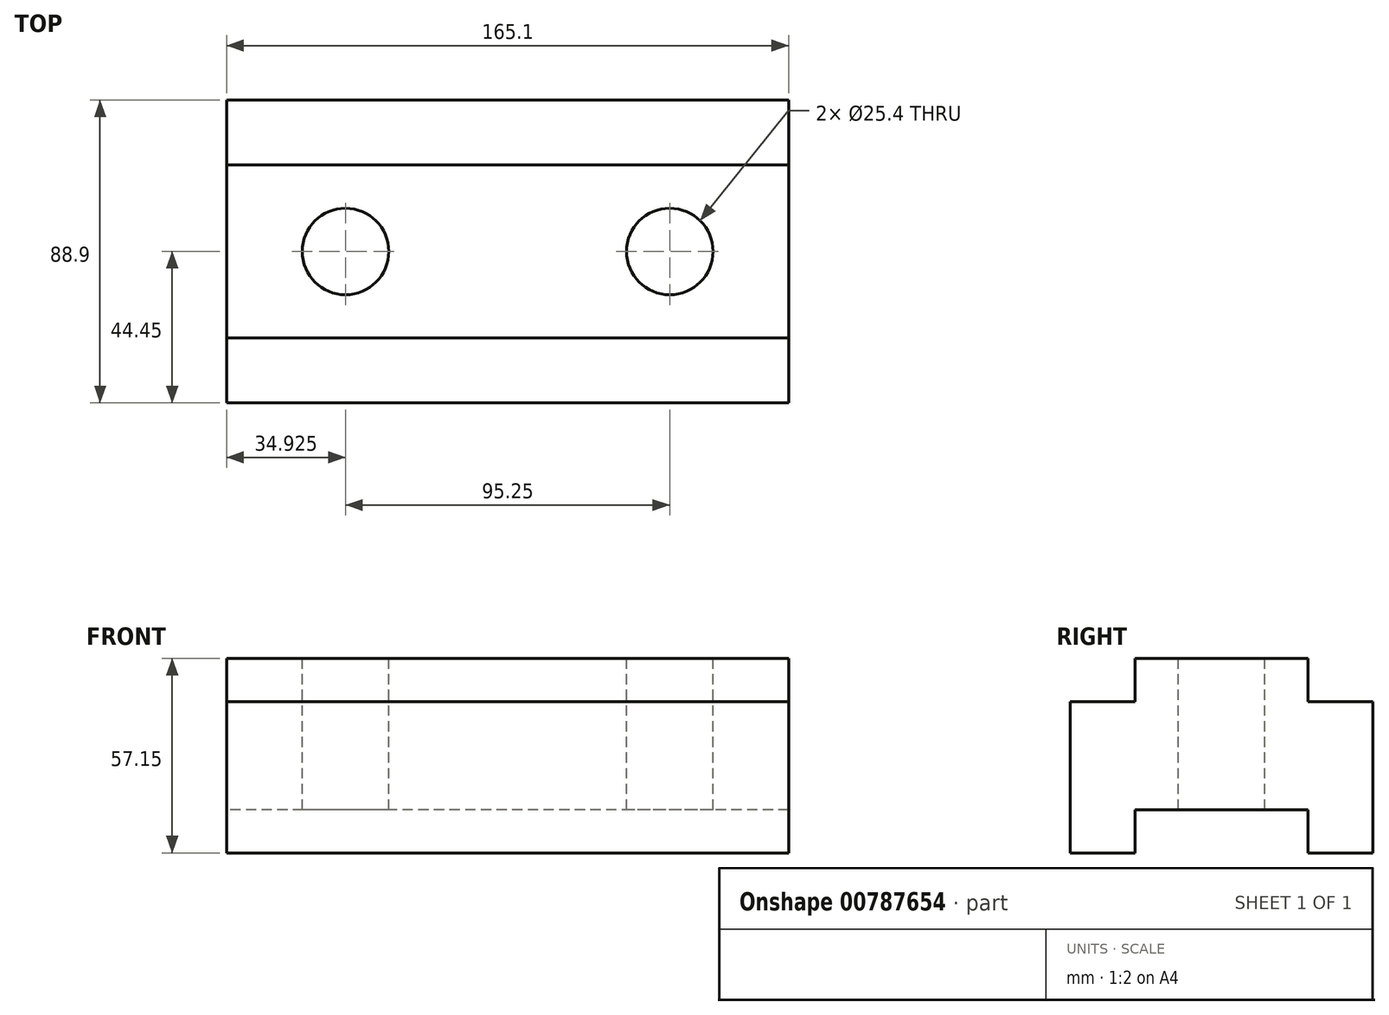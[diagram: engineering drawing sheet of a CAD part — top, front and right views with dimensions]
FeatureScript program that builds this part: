
annotation { "Feature Type Name" : "Feature", "Feature Type Description" : "" }
export const myFeature = defineFeature(function(context is Context, id is Id, definition is map)
    precondition{}
    {
        {
            var Q0;
            Q0=qCreatedBy(makeId("Right.planeOp"),FACE);
            var sketch = newSketch(context, id + "F0", { "sketchPlane" : qUnion([Q0])});
            skLineSegment(sketch, "E0", {"start": v(0, 0) * mm, "end": v(19.05, 0) * mm});
            skLineSegment(sketch, "E1", {"start": v(19.05, 0) * mm, "end": v(19.05, 12.7) * mm});
            skLineSegment(sketch, "E2", {"start": v(19.05, 12.7) * mm, "end": v(69.85, 12.7) * mm});
            skLineSegment(sketch, "E3", {"start": v(69.85, 12.7) * mm, "end": v(69.85, 0) * mm});
            skLineSegment(sketch, "E4", {"start": v(69.85, 0) * mm, "end": v(88.9, 0) * mm});
            skLineSegment(sketch, "E5", {"start": v(88.9, 0) * mm, "end": v(88.9, 44.45) * mm});
            skLineSegment(sketch, "E6", {"start": v(88.9, 44.45) * mm, "end": v(69.85, 44.45) * mm});
            skLineSegment(sketch, "E7", {"start": v(69.85, 44.45) * mm, "end": v(69.85, 57.15) * mm});
            skLineSegment(sketch, "E8", {"start": v(69.85, 57.15) * mm, "end": v(19.05, 57.15) * mm});
            skLineSegment(sketch, "E9", {"start": v(19.05, 57.15) * mm, "end": v(19.05, 44.45) * mm});
            skLineSegment(sketch, "E10", {"start": v(19.05, 44.45) * mm, "end": v(0, 44.45) * mm});
            skLineSegment(sketch, "E11", {"start": v(0, 44.45) * mm, "end": v(0, 0) * mm});
            skSolve(sketch);
        }
        {
            var Q0;
            Q0 = qSketchRegion(id + "F0", true);
            extrude(context, id + "F1", {"entities" : qUnion([Q0]), "depth" : 165.1 * mm, "offsetDistance" : 25.4 * mm});
        }
        {
            var Q0;
            Q0=makeQuery(id+"F1.opExtrude","SWEPT_FACE",FACE,{"disambiguationData":[OSD([sQuery(id+"F0.wireOp",EDGE,"E8")])]});
            var sketch = newSketch(context, id + "F2", { "sketchPlane" : qUnion([Q0])});
            skLineSegment(sketch, "E12", {"start": v(0, 44.45) * mm, "end": v(34.92, 44.45) * mm, "construction": true});
            skLineSegment(sketch, "E13", {"start": v(34.92, 44.45) * mm, "end": v(130.18, 44.45) * mm, "construction": true});
            skLineSegment(sketch, "E14", {"start": v(130.18, 44.45) * mm, "end": v(165.1, 44.45) * mm, "construction": true});
            skCircle(sketch, "E15", {"center": v(34.92, 44.45) * mm, "radius": 12.7 * mm});
            skCircle(sketch, "E16", {"center": v(130.18, 44.45) * mm, "radius": 12.7 * mm});
            skSolve(sketch);
        }
        {
            var Q0;
            Q0=makeQuery(id+"F2.imprint","IMPRINT",FACE,{"disambiguationData":[TD([[makeQuery(id+"F2.imprint","IMPRINT",EDGE,{"derivedFrom":sQuery(id+"F2.wireOp",EDGE,"E15")}),1.0]])]});
            var Q1;
            Q1=makeQuery(id+"F2.imprint","IMPRINT",FACE,{"disambiguationData":[TD([[makeQuery(id+"F2.imprint","IMPRINT",EDGE,{"derivedFrom":sQuery(id+"F2.wireOp",EDGE,"E16")}),1.0]])]});
            extrude(context, id + "F3", {"entities" : qUnion([Q0, Q1]), "operationType" : NewBodyOperationType.REMOVE, "endBound" : BoundingType.THROUGH_ALL, "oppositeDirection" : true, "depth" : 25.4 * mm, "offsetDistance" : 25.4 * mm});
        }
    });
